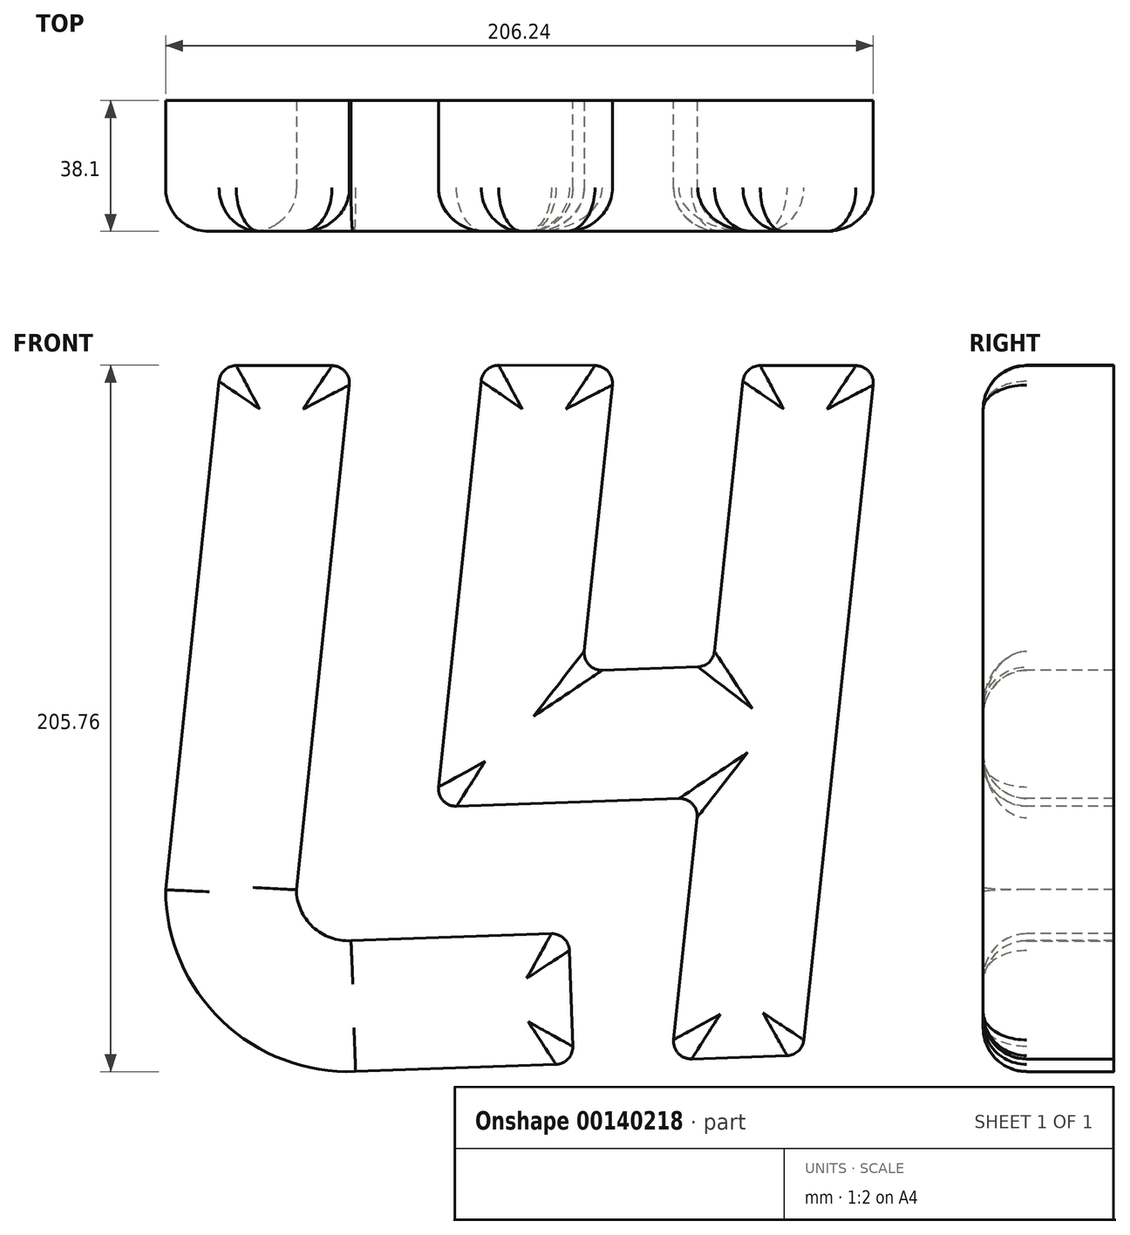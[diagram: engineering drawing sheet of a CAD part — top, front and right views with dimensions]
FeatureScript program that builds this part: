
annotation { "Feature Type Name" : "Feature", "Feature Type Description" : "" }
export const myFeature = defineFeature(function(context is Context, id is Id, definition is map)
    precondition{}
    {
        {
            var Q0;
            Q0=qCreatedBy(makeId("Top.planeOp"),FACE);
            cPlane(context, id + "F0", {"entities" : qUnion([Q0]), "cplaneType" : CPlaneType.OFFSET, "offset" : 76.2 * mm, "width" : 152.4 * mm, "height" : 152.4 * mm});
        }
        {
            var Q0;
            Q0=qCreatedBy(makeId("Front.planeOp"),FACE);
            var sketch = newSketch(context, id + "F1", { "sketchPlane" : qUnion([Q0])});
            skLineSegment(sketch, "E0", {"start": v(0, 76.2) * mm, "end": v(-16.05, -76.46) * mm});
            skLineSegment(sketch, "E1", {"start": v(0, 76.2) * mm, "end": v(0, 0) * mm});
            skSolve(sketch);
        }
        {
            var Q0;
            Q0=qCreatedBy(id+"F0.planeOp",FACE);
            var sketch = newSketch(context, id + "F2", { "sketchPlane" : qUnion([Q0])});
            skLineSegment(sketch, "E2.bottom", {"start": v(-19.05, 19.05) * mm, "end": v(19.05, 19.05) * mm});
            skLineSegment(sketch, "E2.top", {"start": v(-19.05, -19.05) * mm, "end": v(19.05, -19.05) * mm});
            skLineSegment(sketch, "E2.left", {"start": v(-19.05, 19.05) * mm, "end": v(-19.05, -19.05) * mm});
            skLineSegment(sketch, "E2.right", {"start": v(19.05, 19.05) * mm, "end": v(19.05, -19.05) * mm});
            skPoint(sketch, "E2.middle", {"position": v(0, 0) * mm});
            skSolve(sketch);
        }
        {
            var Q0;
            Q0=qCreatedBy(makeId("Top.planeOp"),FACE);
            cPlane(context, id + "F3", {"entities" : qUnion([Q0]), "cplaneType" : CPlaneType.OFFSET, "offset" : 76.2 * mm, "oppositeDirection" : true, "width" : 152.4 * mm, "height" : 152.4 * mm});
        }
        {
            var Q0;
            Q0=makeQuery(id+"F2.imprint","IMPRINT",FACE,{"disambiguationData":[TD([[makeQuery(id+"F2.imprint","IMPRINT",EDGE,{"derivedFrom":sQuery(id+"F2.wireOp",EDGE,"E2.bottom")}),-1.0]])]});
            var Q1;
            Q1=sQuery(id+"F1.wireOp",EDGE,"E0");
            sweep(context, id + "F4", {"profiles" : qUnion([Q0]), "path" : qUnion([Q1])});
        }
        {
            var Q0;
            Q0=qCreatedBy(id+"F3.planeOp",FACE);
            var sketch = newSketch(context, id + "F5", { "sketchPlane" : qUnion([Q0])});
            skLineSegment(sketch, "E3", {"start": v(18.15, -25.8) * mm, "end": v(18.15, 23.83) * mm});
            skSolve(sketch);
        }
        {
            var Q0;
            Q0=makeQuery(id+"F4.opSweep","CAP_FACE",FACE,{"disambiguationData":[OSD([sQuery(id+"F1.wireOp",VERTEX,"E0.end"),sQuery(id+"F2.wireOp",EDGE,"E2.bottom"),sQuery(id+"F2.wireOp",EDGE,"E2.top"),sQuery(id+"F2.wireOp",EDGE,"E2.left"),sQuery(id+"F2.wireOp",EDGE,"E2.right")])],"isStart":false});
            var Q1;
            Q1=sQuery(id+"F5.wireOp",EDGE,"E3");
            revolve(context, id + "F6", {"operationType" : NewBodyOperationType.ADD, "entities" : qUnion([Q0]), "axis" : qUnion([Q1]), "revolveType" : RevolveType.ONE_DIRECTION, "oppositeDirection" : true, "angle" : 92 * degree});
        }
        {
            var Q0;
            Q0=makeQuery(id+"F6.opRevolve","CAP_FACE",FACE,{"disambiguationData":[OSD([sQuery(id+"F1.wireOp",VERTEX,"E0.end"),sQuery(id+"F2.wireOp",EDGE,"E2.bottom"),sQuery(id+"F2.wireOp",EDGE,"E2.top"),sQuery(id+"F2.wireOp",EDGE,"E2.left"),sQuery(id+"F2.wireOp",EDGE,"E2.right")])],"isStart":false});
            extrude(context, id + "F7", {"entities" : qUnion([Q0]), "operationType" : NewBodyOperationType.ADD, "depth" : 63.5 * mm});
        }
        {
            var Q0;
            Q0=qCreatedBy(makeId("Front.planeOp"),FACE);
            cPlane(context, id + "F8", {"entities" : qUnion([Q0]), "cplaneType" : CPlaneType.OFFSET, "offset" : 19.05 * mm, "oppositeDirection" : true, "width" : 152.4 * mm, "height" : 152.4 * mm});
        }
        {
            var Q0;
            Q0=qCreatedBy(id+"F8.planeOp",FACE);
            var sketch = newSketch(context, id + "F9", { "sketchPlane" : qUnion([Q0])});
            skLineSegment(sketch, "E4.0.0", {"start": v(19.05, 76.2) * mm, "end": v(3, -76.46) * mm});
            skArc(sketch, "E4.0.1", {"start": v(3, -76.46) * mm, "mid": v(7.82, -87.28) * mm, "end": v(18.94, -91.33) * mm});
            skLineSegment(sketch, "E4.0.2", {"start": v(18.94, -91.33) * mm, "end": v(82.4, -89.11) * mm});
            skLineSegment(sketch, "E4.0.3", {"start": v(82.4, -89.11) * mm, "end": v(83.73, -127.19) * mm});
            skLineSegment(sketch, "E4.0.4", {"start": v(83.73, -127.19) * mm, "end": v(20.27, -129.4) * mm});
            skArc(sketch, "E4.0.5", {"start": v(20.27, -129.4) * mm, "mid": v(-18.65, -114.69) * mm, "end": v(-35.1, -76.46) * mm});
            skLineSegment(sketch, "E4.0.6", {"start": v(-35.1, -76.46) * mm, "end": v(-19.05, 76.2) * mm});
            skLineSegment(sketch, "E4.0.7", {"start": v(-19.05, 76.2) * mm, "end": v(19.05, 76.2) * mm});
            skLineSegment(sketch, "E5", {"start": v(11.04, 0) * mm, "end": v(48.93, -3.98) * mm, "construction": true});
            skLineSegment(sketch, "E6", {"start": v(48.93, -3.98) * mm, "end": v(57.37, 76.32) * mm});
            skLineSegment(sketch, "E7", {"start": v(43.85, -52.34) * mm, "end": v(120.38, -49.66) * mm});
            skLineSegment(sketch, "E8", {"start": v(124.4, -11.4) * mm, "end": v(86.32, -12.73) * mm});
            skLineSegment(sketch, "E9", {"start": v(86.32, -12.73) * mm, "end": v(95.67, 76.2) * mm});
            skLineSegment(sketch, "E10", {"start": v(54.62, 50.1) * mm, "end": v(92.5, 46.12) * mm, "construction": true});
            skLineSegment(sketch, "E11", {"start": v(95.74, -12.4) * mm, "end": v(97.07, -50.48) * mm, "construction": true});
            skLineSegment(sketch, "E12", {"start": v(48.93, -3.98) * mm, "end": v(43.85, -52.34) * mm});
            skLineSegment(sketch, "E13", {"start": v(61.83, -51.7) * mm, "end": v(63.16, -89.78) * mm, "construction": true});
            skLineSegment(sketch, "E14", {"start": v(57.37, 76.32) * mm, "end": v(95.67, 76.2) * mm});
            skLineSegment(sketch, "E15", {"start": v(124.4, -11.4) * mm, "end": v(133.6, 76.2) * mm});
            skLineSegment(sketch, "E16", {"start": v(133.6, 76.2) * mm, "end": v(171.7, 76.2) * mm});
            skLineSegment(sketch, "E17", {"start": v(120.38, -49.66) * mm, "end": v(112.36, -125.96) * mm});
            skLineSegment(sketch, "E18", {"start": v(112.36, -125.96) * mm, "end": v(150.44, -124.63) * mm});
            skLineSegment(sketch, "E19", {"start": v(150.44, -124.63) * mm, "end": v(171.7, 76.2) * mm});
            skSolve(sketch);
        }
        {
            var Q0;
            Q0=makeQuery(id+"F9.imprint","IMPRINT",FACE,{"disambiguationData":[TD([[makeQuery(id+"F9.imprint","IMPRINT",EDGE,{"derivedFrom":sQuery(id+"F9.wireOp",EDGE,"E6")}),-1.0]])]});
            extrude(context, id + "F10", {"entities" : qUnion([Q0]), "depth" : 38.1 * mm});
        }
        {
            var Q0;
            Q0=makeQuery(id+"F4.opSweep","SWEPT_EDGE",EDGE,{"disambiguationData":[OSD([sQuery(id+"F1.wireOp",EDGE,"E0"),sQuery(id+"F2.wireOp",EDGE,"E2.top"),sQuery(id+"F2.wireOp",EDGE,"E2.left")])]});
            var Q1;
            Q1=makeQuery(id+"F6.opRevolve","SWEPT_EDGE",EDGE,{"disambiguationData":[OSD([sQuery(id+"F1.wireOp",EDGE,"E0"),sQuery(id+"F2.wireOp",EDGE,"E2.top"),sQuery(id+"F2.wireOp",EDGE,"E2.left")])]});
            var Q2;
            Q2=makeQuery(id+"F7.opExtrude","CAP_EDGE",EDGE,{"disambiguationData":[OSD([sQuery(id+"F1.wireOp",VERTEX,"E0.end"),sQuery(id+"F2.wireOp",EDGE,"E2.top")])],"isStart":false});
            var Q3;
            Q3=makeQuery(id+"F7.opExtrude","SWEPT_EDGE",EDGE,{"disambiguationData":[OSD([sQuery(id+"F1.wireOp",EDGE,"E0"),sQuery(id+"F2.wireOp",EDGE,"E2.top"),sQuery(id+"F2.wireOp",EDGE,"E2.right")])]});
            var Q4;
            Q4=makeQuery(id+"F6.opRevolve","SWEPT_EDGE",EDGE,{"disambiguationData":[OSD([sQuery(id+"F1.wireOp",EDGE,"E0"),sQuery(id+"F2.wireOp",EDGE,"E2.top"),sQuery(id+"F2.wireOp",EDGE,"E2.right")])]});
            var Q5;
            Q5=makeQuery(id+"F4.opSweep","SWEPT_EDGE",EDGE,{"disambiguationData":[OSD([sQuery(id+"F1.wireOp",EDGE,"E0"),sQuery(id+"F2.wireOp",EDGE,"E2.top"),sQuery(id+"F2.wireOp",EDGE,"E2.right")])]});
            var Q6;
            Q6=makeQuery(id+"F4.opSweep","CAP_EDGE",EDGE,{"disambiguationData":[OSD([sQuery(id+"F1.wireOp",VERTEX,"E0.start"),sQuery(id+"F2.wireOp",EDGE,"E2.top")])],"isStart":true});
            var Q7;
            Q7=makeQuery(id+"F10.opExtrude","CAP_EDGE",EDGE,{"disambiguationData":[OSD([sQuery(id+"F9.wireOp",EDGE,"E7")])],"isStart":false});
            var Q8;
            Q8=makeQuery(id+"F10.opExtrude","CAP_EDGE",EDGE,{"disambiguationData":[OSD([sQuery(id+"F9.wireOp",EDGE,"E6"),sQuery(id+"F9.wireOp",EDGE,"E12")])],"isStart":false});
            var Q9;
            Q9=makeQuery(id+"F10.opExtrude","CAP_EDGE",EDGE,{"disambiguationData":[OSD([sQuery(id+"F9.wireOp",EDGE,"E9")])],"isStart":false});
            var Q10;
            Q10=makeQuery(id+"F10.opExtrude","CAP_EDGE",EDGE,{"disambiguationData":[OSD([sQuery(id+"F9.wireOp",EDGE,"E8")])],"isStart":false});
            var Q11;
            Q11=makeQuery(id+"F10.opExtrude","CAP_EDGE",EDGE,{"disambiguationData":[OSD([sQuery(id+"F9.wireOp",EDGE,"E15")])],"isStart":false});
            var Q12;
            Q12=makeQuery(id+"F10.opExtrude","CAP_EDGE",EDGE,{"disambiguationData":[OSD([sQuery(id+"F9.wireOp",EDGE,"E19")])],"isStart":false});
            var Q13;
            Q13=makeQuery(id+"F10.opExtrude","CAP_EDGE",EDGE,{"disambiguationData":[OSD([sQuery(id+"F9.wireOp",EDGE,"E18")])],"isStart":false});
            var Q14;
            Q14=makeQuery(id+"F10.opExtrude","CAP_EDGE",EDGE,{"disambiguationData":[OSD([sQuery(id+"F9.wireOp",EDGE,"E17")])],"isStart":false});
            var Q15;
            Q15=makeQuery(id+"F10.opExtrude","CAP_EDGE",EDGE,{"disambiguationData":[OSD([sQuery(id+"F9.wireOp",EDGE,"E16")])],"isStart":false});
            var Q16;
            Q16=makeQuery(id+"F10.opExtrude","CAP_EDGE",EDGE,{"disambiguationData":[OSD([sQuery(id+"F9.wireOp",EDGE,"E14")])],"isStart":false});
            fillet(context, id + "F11", {"entities" : qUnion([Q0, Q1, Q2, Q3, Q4, Q5, Q6, Q7, Q8, Q9, Q10, Q11, Q12, Q13, Q14, Q15, Q16]), "radius" : 12.7 * mm, "tangentPropagation" : true, "allowEdgeOverflow" : false});
        }
        {
            var Q0;
            Q0=makeQuery(id+"F4.opSweep","CAP_EDGE",EDGE,{"disambiguationData":[OSD([sQuery(id+"F1.wireOp",VERTEX,"E0.start"),sQuery(id+"F2.wireOp",EDGE,"E2.left")])],"isStart":true});
            var Q1;
            Q1=makeQuery(id+"F4.opSweep","CAP_EDGE",EDGE,{"disambiguationData":[OSD([sQuery(id+"F1.wireOp",VERTEX,"E0.start"),sQuery(id+"F2.wireOp",EDGE,"E2.right")])],"isStart":true});
            var Q2;
            Q2=makeQuery(id+"F7.opExtrude","CAP_EDGE",EDGE,{"disambiguationData":[OSD([sQuery(id+"F1.wireOp",VERTEX,"E0.end"),sQuery(id+"F2.wireOp",EDGE,"E2.right")])],"isStart":false});
            var Q3;
            Q3=makeQuery(id+"F7.opExtrude","CAP_EDGE",EDGE,{"disambiguationData":[OSD([sQuery(id+"F1.wireOp",VERTEX,"E0.end"),sQuery(id+"F2.wireOp",EDGE,"E2.left")])],"isStart":false});
            var Q4;
            Q4=makeQuery(id+"F10.opExtrude","SWEPT_EDGE",EDGE,{"disambiguationData":[OSD([sQuery(id+"F9.wireOp",EDGE,"E6"),sQuery(id+"F9.wireOp",EDGE,"E14")])]});
            var Q5;
            Q5=makeQuery(id+"F10.opExtrude","SWEPT_EDGE",EDGE,{"disambiguationData":[OSD([sQuery(id+"F9.wireOp",EDGE,"E9"),sQuery(id+"F9.wireOp",EDGE,"E14")])]});
            var Q6;
            Q6=makeQuery(id+"F10.opExtrude","SWEPT_EDGE",EDGE,{"disambiguationData":[OSD([sQuery(id+"F9.wireOp",EDGE,"E15"),sQuery(id+"F9.wireOp",EDGE,"E16")])]});
            var Q7;
            Q7=makeQuery(id+"F10.opExtrude","SWEPT_EDGE",EDGE,{"disambiguationData":[OSD([sQuery(id+"F9.wireOp",EDGE,"E16"),sQuery(id+"F9.wireOp",EDGE,"E19")])]});
            var Q8;
            Q8=makeQuery(id+"F10.opExtrude","SWEPT_EDGE",EDGE,{"disambiguationData":[OSD([sQuery(id+"F9.wireOp",EDGE,"E18"),sQuery(id+"F9.wireOp",EDGE,"E19")])]});
            var Q9;
            Q9=makeQuery(id+"F10.opExtrude","SWEPT_EDGE",EDGE,{"disambiguationData":[OSD([sQuery(id+"F9.wireOp",EDGE,"E17"),sQuery(id+"F9.wireOp",EDGE,"E18")])]});
            var Q10;
            Q10=makeQuery(id+"F10.opExtrude","SWEPT_EDGE",EDGE,{"disambiguationData":[OSD([sQuery(id+"F9.wireOp",EDGE,"E7"),sQuery(id+"F9.wireOp",EDGE,"E12")])]});
            var Q11;
            Q11=makeQuery(id+"F10.opExtrude","SWEPT_EDGE",EDGE,{"disambiguationData":[OSD([sQuery(id+"F9.wireOp",EDGE,"E7"),sQuery(id+"F9.wireOp",EDGE,"E17")])]});
            var Q12;
            Q12=makeQuery(id+"F10.opExtrude","SWEPT_EDGE",EDGE,{"disambiguationData":[OSD([sQuery(id+"F9.wireOp",EDGE,"E8"),sQuery(id+"F9.wireOp",EDGE,"E9")])]});
            var Q13;
            Q13=makeQuery(id+"F10.opExtrude","SWEPT_EDGE",EDGE,{"disambiguationData":[OSD([sQuery(id+"F9.wireOp",EDGE,"E8"),sQuery(id+"F9.wireOp",EDGE,"E15")])]});
            fillet(context, id + "F12", {"entities" : qUnion([Q0, Q1, Q2, Q3, Q4, Q5, Q6, Q7, Q8, Q9, Q10, Q11, Q12, Q13]), "radius" : 5.08 * mm, "tangentPropagation" : true, "allowEdgeOverflow" : false});
        }
    });
